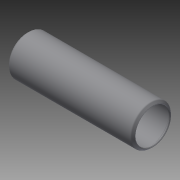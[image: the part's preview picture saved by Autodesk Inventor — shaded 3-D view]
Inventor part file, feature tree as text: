
AUTODESK INVENTOR PART (.ipt)
format: ipt  version: 2014 SP2 (Build 180246200, 246)  size: 141,312 bytes
history: native  units: in
note: dims shown in document units (in); Inventor stores cm internally (conversion verified against a paired STEP export)
features: other x42, revolve x1, sketch x1
ambient origin geometry x8: Origin, YZ Plane, XZ Plane, XY Plane, X Axis, Y Axis, Z Axis, Center Point
bodies: Solid1 (feature_tree)
feature tree (44):
  revolve  "Revolution1"  [1 undecoded]
  other  "cp1_XY"
  other  "cp1_YZ"
  other  "cp1_ZX"
  other  "cp1_X"
  other  "cp1_Y"
  other  "cp1_Z"
  other  "cp1_Center"
  other  "cp2_XY"
  other  "cp2_YZ"
  other  "cp2_ZX"
  other  "cp2_X"
  other  "cp2_Y"
  other  "cp2_Z"
  other  "cp2_Center"
  other  "cp3_XY"
  other  "cp3_YZ"
  other  "cp3_ZX"
  other  "cp3_X"
  other  "cp3_Y"
  other  "cp3_Z"
  other  "cp3_Center"
  other  "cp4_XY"
  other  "cp4_YZ"
  other  "cp4_ZX"
  other  "cp4_X"
  other  "cp4_Y"
  other  "cp4_Z"
  other  "cp4_Center"
  other  "tube_front_XY"
  other  "tube_front_YZ"
  other  "tube_front_ZX"
  other  "tube_front_X"
  other  "tube_front_Y"
  other  "tube_front_Z"
  other  "tube_front_Center"
  other  "tube_rear_XY"
  other  "tube_rear_YZ"
  other  "tube_rear_ZX"
  other  "tube_rear_X"
  other  "tube_rear_Y"
  other  "tube_rear_Z"
  other  "tube_rear_Center"
  sketch  "Sketch_1"  dims[d0=360.0deg]
note: 1 required parameter value undecoded (feature->parameter linkage not recoverable at this tier; creation-order binding heuristic only, values carry confidence <= 0.55)
